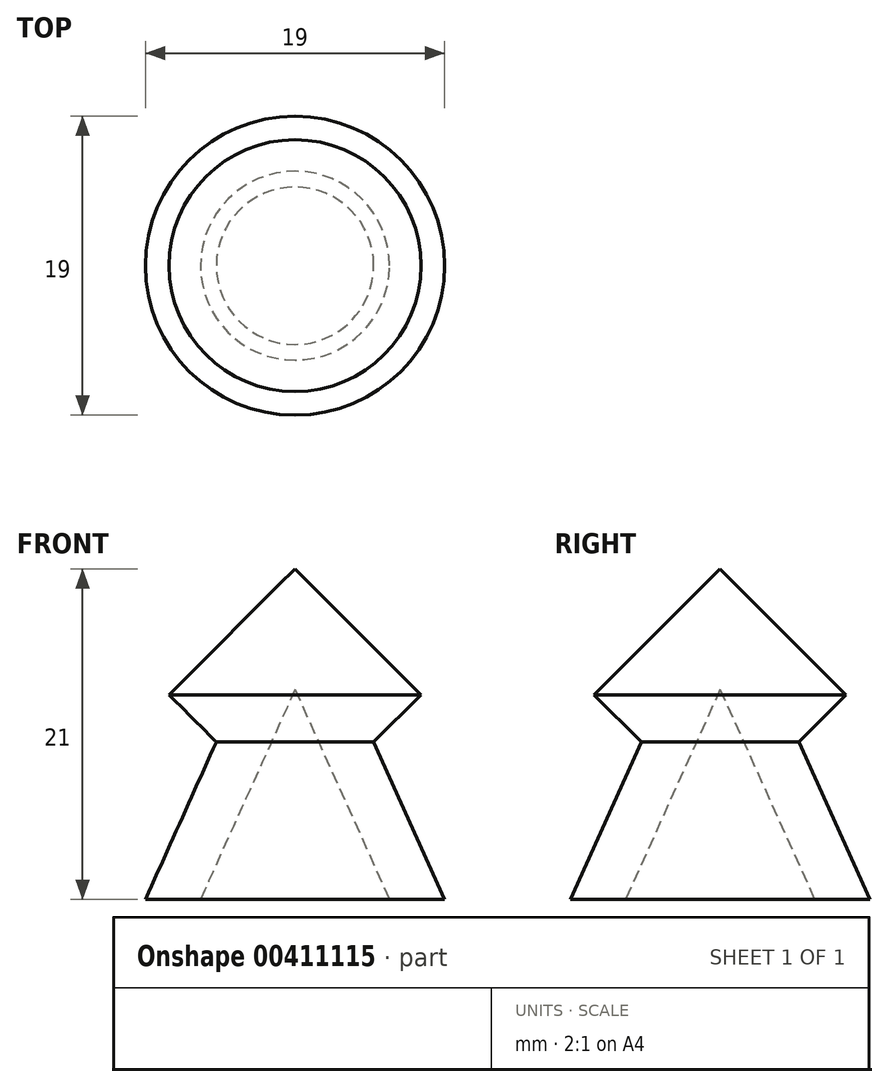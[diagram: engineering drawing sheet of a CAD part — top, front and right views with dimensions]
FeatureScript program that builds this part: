
annotation { "Feature Type Name" : "Feature", "Feature Type Description" : "" }
export const myFeature = defineFeature(function(context is Context, id is Id, definition is map)
    precondition{}
    {
        {
            var Q0;
            Q0=qCreatedBy(makeId("Front.planeOp"),FACE);
            var sketch = newSketch(context, id + "F0", { "sketchPlane" : qUnion([Q0])});
            skLineSegment(sketch, "E0", {"start": v(-6, 0) * mm, "end": v(-9.5, 0) * mm});
            skLineSegment(sketch, "E1", {"start": v(-9.5, 0) * mm, "end": v(-5, 10) * mm});
            skLineSegment(sketch, "E2", {"start": v(-5, 10) * mm, "end": v(-8, 13) * mm});
            skLineSegment(sketch, "E3", {"start": v(-8, 13) * mm, "end": v(0, 21) * mm});
            skLineSegment(sketch, "E4", {"start": v(0, 21) * mm, "end": v(0, 13.33) * mm});
            skLineSegment(sketch, "E5", {"start": v(-6, 0) * mm, "end": v(0, 13.33) * mm});
            skLineSegment(sketch, "E6", {"start": v(0, -3.1) * mm, "end": v(0, 25.5) * mm});
            skSolve(sketch);
        }
        {
            var Q0;
            Q0=makeQuery(id+"F0.imprint","IMPRINT",FACE,{"disambiguationData":[TD([[makeQuery(id+"F0.imprint","IMPRINT",EDGE,{"derivedFrom":sQuery(id+"F0.wireOp",EDGE,"E0")}),-1.0]])]});
            var Q1;
            Q1=sQuery(id+"F0.wireOp",EDGE,"E6");
            revolve(context, id + "F1", {"entities" : qUnion([Q0]), "axis" : qUnion([Q1]), "revolveType" : RevolveType.FULL});
        }
    });
